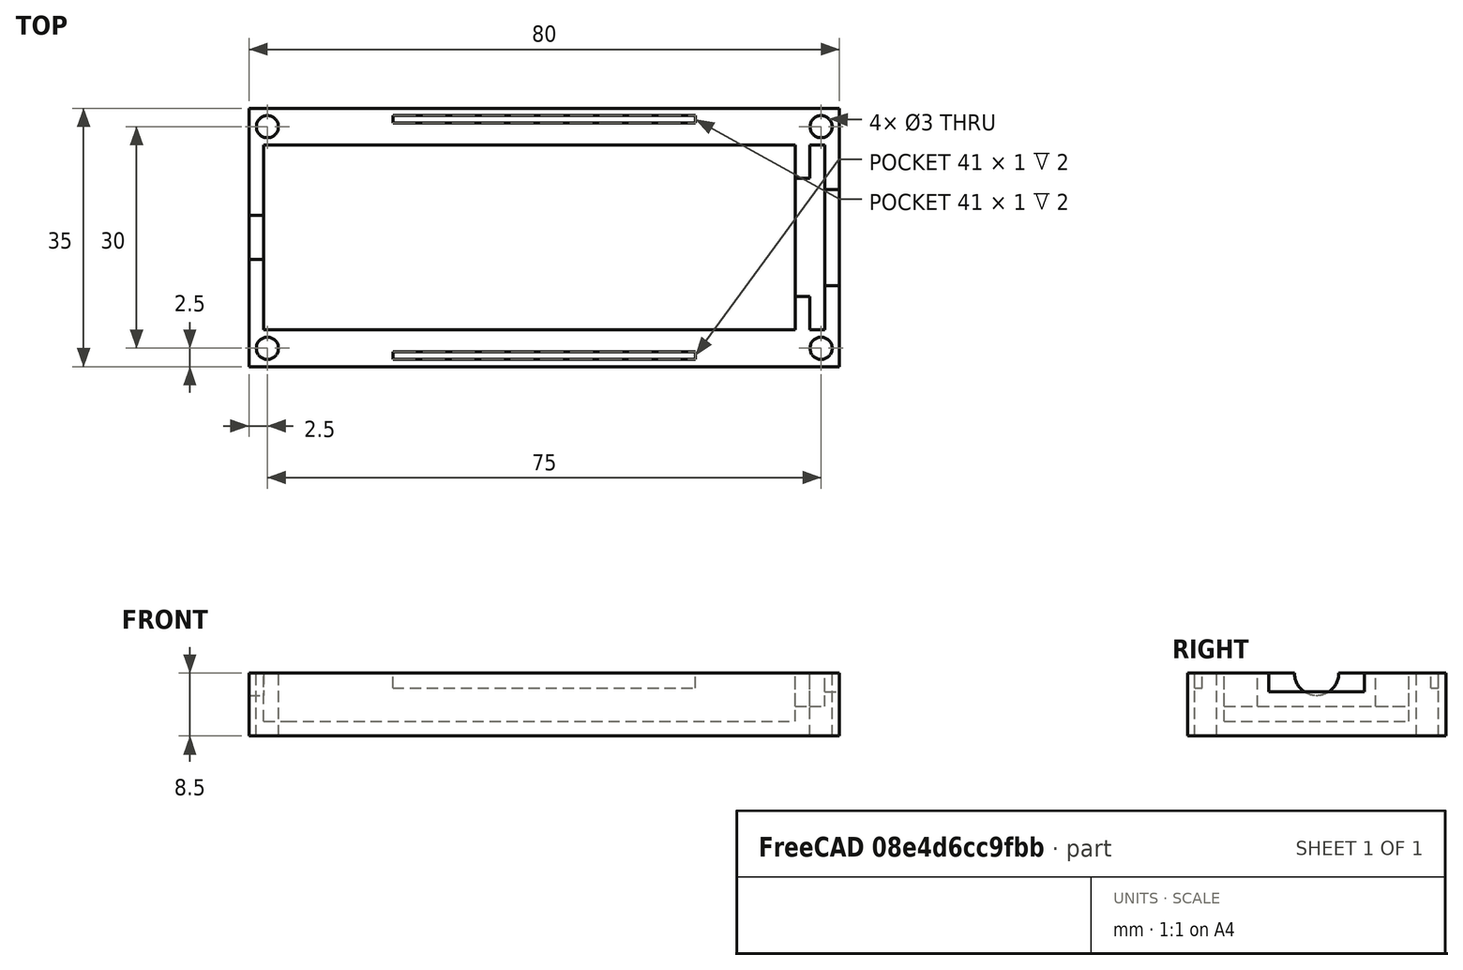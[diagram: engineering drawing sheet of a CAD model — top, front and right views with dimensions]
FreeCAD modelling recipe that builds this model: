
FCSTD DOCUMENT  (FreeCAD 0.17R13509 (Git))
Label: USB2A_1
License: All rights reserved
LicenseURL: http://en.wikipedia.org/wiki/All_rights_reserved
objects: Part::Cut×12, Part::Box×8, Part::Cylinder×5
note: 25 computed .brp shape members not serialized (recipe doc carries the construction recipe); baked Part::Feature solids carry a one-line shape summary decoded from their .brp

FEATURE [Part::Box] Box  label="外壳"
  AttacherType = Attacher::AttachEngine3D
  Height = 8.5
  Length = 80
  Width = 35
FEATURE [Part::Box] Box001  label="内胆"
  AttacherType = Attacher::AttachEngine3D
  Height = 13
  Length = 69
  Placement = pos=(5,5,2) rot=(0,0,1;0rad)
  Width = 25
FEATURE [Part::Cylinder] Cylinder  label="圆柱体"
  Angle = 360
  AttacherType = Attacher::AttachEngine3D
  Height = 2
  Placement = pos=(0,17.5,8.5) rot=(0,1,0;1.5708rad)
  Radius = 3
FEATURE [Part::Box] Box002  label="卡槽"
  AttacherType = Attacher::AttachEngine3D
  Height = 9
  Length = 2
  Placement = pos=(76,5,4) rot=(0,0,1;0rad)
  Width = 25
FEATURE [Part::Box] Box003  label="U口"
  AttacherType = Attacher::AttachEngine3D
  Height = 5
  Length = 2
  Placement = pos=(78,11,6) rot=(0,0,1;0rad)
  Width = 13
FEATURE [Part::Box] Box004  label="立方体003"
  AttacherType = Attacher::AttachEngine3D
  Height = 9
  Length = 2
  Placement = pos=(74,9.5,4) rot=(0,0,1;0rad)
  Width = 16
FEATURE [Part::Box] Box005  label="立方体"
  AttacherType = Attacher::AttachEngine3D
  Height = 10
  Length = 3
  Placement = pos=(2,5,2) rot=(0,0,1;0rad)
  Width = 25
FEATURE [Part::Cylinder] Cylinder001  label="螺孔1"
  Angle = 360
  AttacherType = Attacher::AttachEngine3D
  Height = 10
  Placement = pos=(2.5,2.5,0) rot=(0,0,1;0rad)
  Radius = 1.5
FEATURE [Part::Cylinder] Cylinder002  label="螺孔2"
  Angle = 360
  AttacherType = Attacher::AttachEngine3D
  Height = 10
  Placement = pos=(77.5,2.5,0) rot=(0,0,1;0rad)
  Radius = 1.5
FEATURE [Part::Cylinder] Cylinder003  label="螺孔3"
  Angle = 360
  AttacherType = Attacher::AttachEngine3D
  Height = 10
  Placement = pos=(77.5,32.5,0) rot=(0,0,1;0rad)
  Radius = 1.5
FEATURE [Part::Cylinder] Cylinder004  label="螺孔4"
  Angle = 360
  AttacherType = Attacher::AttachEngine3D
  Height = 10
  Placement = pos=(2.5,32.5,0) rot=(0,0,1;0rad)
  Radius = 1.5
FEATURE [Part::Box] Box008  label="卡壁凹1"
  AttacherType = Attacher::AttachEngine3D
  Height = 2
  Length = 41
  Placement = pos=(19.5,33,6.5) rot=(0,0,1;0rad)
  Width = 1
FEATURE [Part::Box] Box009  label="卡壁凹2"
  AttacherType = Attacher::AttachEngine3D
  Height = 2
  Length = 41
  Placement = pos=(19.5,1,6.5) rot=(0,0,1;0rad)
  Width = 1
FEATURE [Part::Cut] Cut
  Base = -> Box
  Tool = -> Box001
FEATURE [Part::Cut] Cut001
  Base = -> Cut
  Tool = -> Cylinder
FEATURE [Part::Cut] Cut002
  Base = -> Cut001
  Tool = -> Box002
FEATURE [Part::Cut] Cut003
  Base = -> Cut002
  Tool = -> Box003
FEATURE [Part::Cut] Cut004
  Base = -> Cut003
  Tool = -> Box004
FEATURE [Part::Cut] Cut005
  Base = -> Cut004
  Tool = -> Box005
FEATURE [Part::Cut] Cut006
  Base = -> Cut005
  Tool = -> Cylinder001
FEATURE [Part::Cut] Cut007
  Base = -> Cut006
  Tool = -> Cylinder002
FEATURE [Part::Cut] Cut008
  Base = -> Cut007
  Tool = -> Cylinder003
FEATURE [Part::Cut] Cut009
  Base = -> Cut008
  Tool = -> Cylinder004
FEATURE [Part::Cut] Cut010
  Base = -> Cut009
  Tool = -> Box008
FEATURE [Part::Cut] Cut011
  Base = -> Cut010
  Tool = -> Box009
